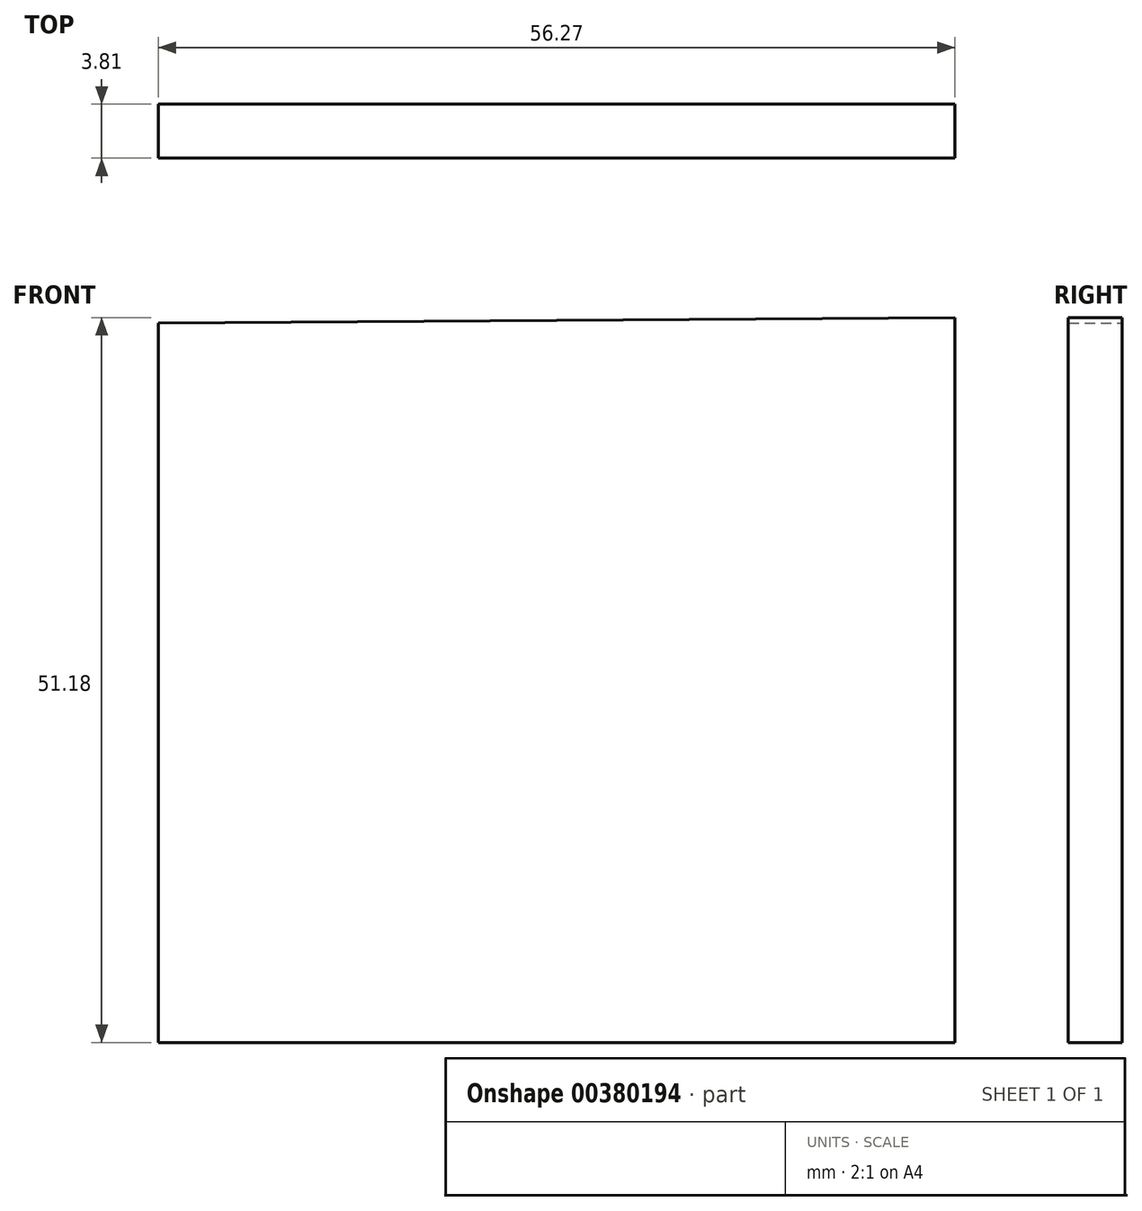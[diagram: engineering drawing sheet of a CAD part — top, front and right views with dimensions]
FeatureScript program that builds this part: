
annotation { "Feature Type Name" : "Feature", "Feature Type Description" : "" }
export const myFeature = defineFeature(function(context is Context, id is Id, definition is map)
    precondition{}
    {
        {
            var Q0;
            Q0=qCreatedBy(makeId("Front.planeOp"),FACE);
            var sketch = newSketch(context, id + "F0", { "sketchPlane" : qUnion([Q0])});
            skLineSegment(sketch, "E0", {"start": v(-36.83, 29.29) * mm, "end": v(-36.83, -21.51) * mm});
            skLineSegment(sketch, "E1", {"start": v(-36.83, -21.51) * mm, "end": v(19.44, -21.51) * mm});
            skLineSegment(sketch, "E2", {"start": v(19.44, -21.51) * mm, "end": v(19.44, 29.67) * mm});
            skLineSegment(sketch, "E3", {"start": v(19.44, 29.67) * mm, "end": v(-36.83, 29.29) * mm});
            skSolve(sketch);
        }
        {
            var Q0;
            Q0 = qSketchRegion(id + "F0", true);
            var Q1;
            Q1=makeQuery(id+"F0.imprint","IMPRINT",FACE,{"disambiguationData":[TD([[makeQuery(id+"F0.imprint","IMPRINT",EDGE,{"derivedFrom":sQuery(id+"F0.wireOp",EDGE,"E0")}),1.0]])]});
            extrude(context, id + "F1", {"entities" : qUnion([Q0, Q1]), "depth" : 3.8 * mm});
        }
    });
